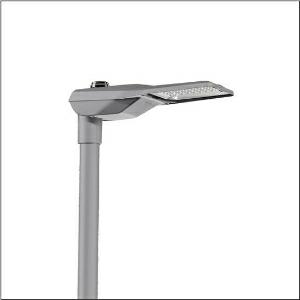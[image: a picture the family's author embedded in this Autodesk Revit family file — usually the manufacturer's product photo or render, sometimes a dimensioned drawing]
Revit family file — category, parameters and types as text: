
# Revit family: streetlight_sl_21_mini___st1_5a_5xe6p37n08hb_7a86
name_source: partatom
category: Lighting Fixtures
units: mm (PartAtom-declared; Revit-internal decimal feet)

## family parameters
Cut with Voids When Loaded = No
Host = Face
Light Source = No
Part Type = Normal
Room Calculation Point = No
Round Connector Dimension = Use Diameter
Shared = No

## types (1)
- --- (1 x LED, 8890 lm, 66 W, 3000K)
    Apparent Load = 66 VA
    CIE Flux Codes = 22 53 95 100 100
    Color Rendering = 70
    Color Temperature = 3000K
    Default Elevation = 1800 mm
    Description = Streetlight SL 21 mini, mast luminaire, primary light control with lens, of PMMA, primary optical cover: cover, of toughened safety glass, transparent, light distribution: ST1.5a, light emission: direct distribution, primary light characteristic: asymmetric, installation type: side-entry, LED, 3G 1.5mm², High Power LED, rated luminous flux: 8.890lm, luminous efficacy: 135lm/W, light colour: 730, colour temperature: 3000K, control gear: NEMA (7pin), control: overheat protection, pre-setting: linear dimming characteristic, constant luminous flux control, time-dependent luminous flux control, flexible luminous flux parameterisation, mains connection: 230..240V, AC, 50/60Hz, connection cable pre-assembled, cable length: 8,5m, wiring characteristics: H07RN-F, start of lifetime: 66W, end of service life: 69W, reduction: 30W, luminaire housing, of diecast aluminium (EN AC-44300), powder-coated, Siteco® metallic grey (DB 702S), corrosivity category C5 mid according to DIN EN ISO 12944, multi-level sealing system, sealing non-destructively replaceable, inclination adjustable: 0°, 5°, 10°, 15°, length: 628mm, width: 235mm, height: 110mm, spigot size: 42mm (side-entry), mounting height: 4..8m, protection rating (complete): IP66, insulation class (complete): insulation class I (protective earthing), certification: CE, ENEC, ENEC+, VDE, impact resistance: IK10, permissible operating ambient temperature for outdoor applications: -40..+50°C, standard-compliant lighting for roads and squares, packaging unit: 1 piece

Light Distribution: ST1.5a
    Height = 110 mm
    Lamp = 1 x LED
    Lamp Light Flux = 8890 lm
    Lamp Power = 66 W
    Lamp count = 1
    Length = 625 mm
    Luminous efficacy = 135 lm/W
    Manufacturer = Siteco
    ModVariant = No
    Model = 5XE6P37N08HB
    Number of Poles = 1
    OnlyDefault = Yes
    Power Factor = 1
    Product Name = Streetlight SL 21 mini | ST1.5a
    Product group = mast luminaire | pylon top
    ProductGroupID = 6100
    Protection Class = Protection class I
    Protection Degree = IP 66
    RLX_Detail_Level = 1
    RLX_Emergency_Light_Flux = 0 lm
    RLX_Emergency_Type = 0
    RLX_Emergency_Type_DB = No
    RlxData = <blob elided: 29681 chars, md5=ab34430e>
    Socket = socket
    Standby Power = 0 W
    System Light Flux = 8890 lm
    System Power = 66 W
    Type Comments = factory setting: luminous flux: 100 % | dim-lin: 254 | 670 mA
    Type Image = l_1294379.jpg
    URL = http://relux.com
    VarID = @adj_133618
    Voltage = 0 V
    Weight = 0.00 kg
    Width = 234 mm

## geometry (parser evidence)
native form markers: Blend x4, Sweep x11
no freeform markers — native parametric forms only
